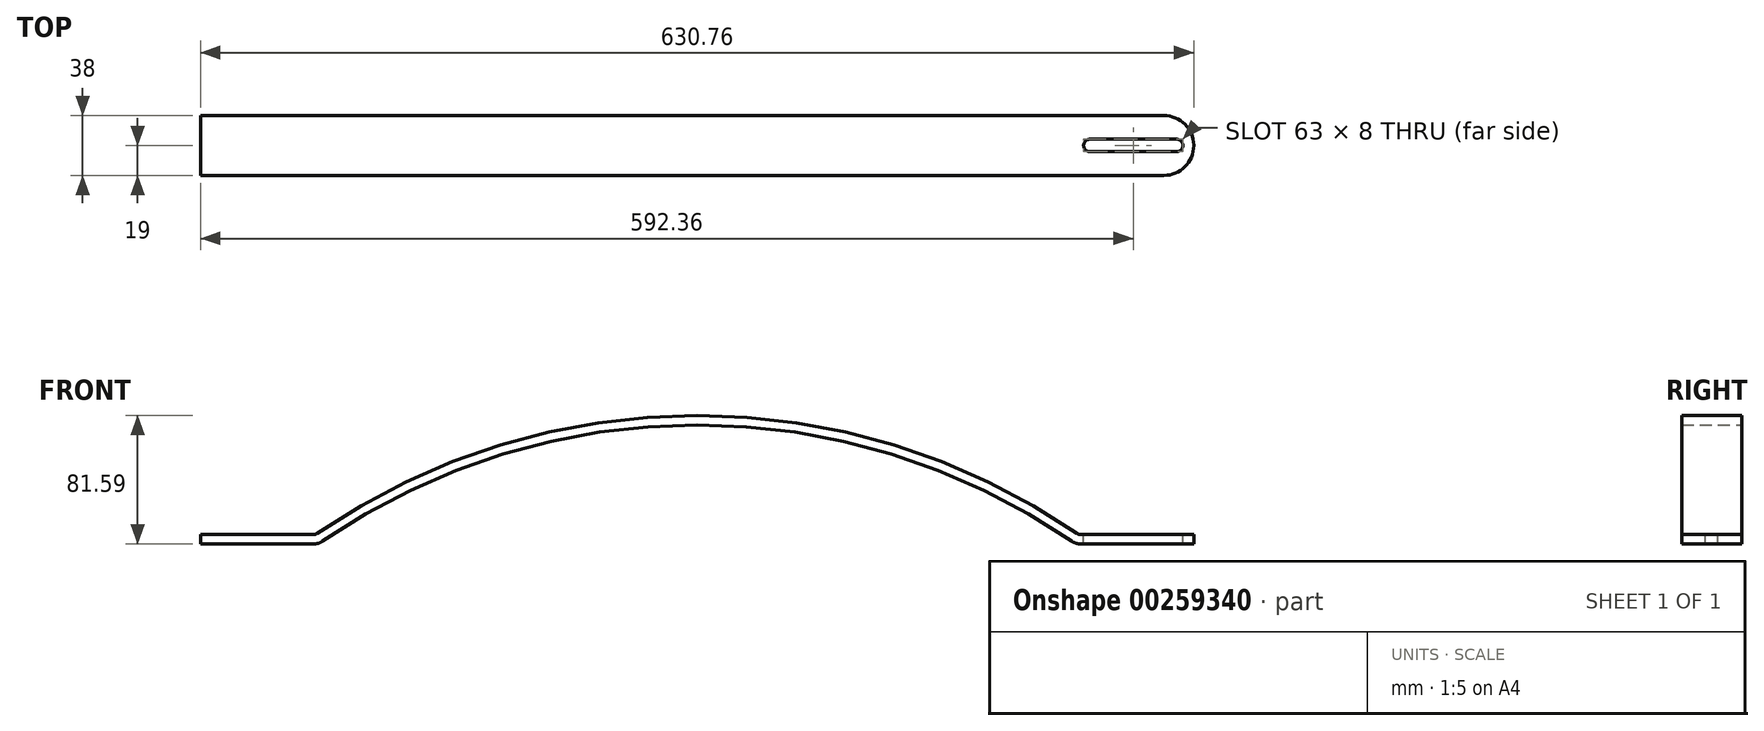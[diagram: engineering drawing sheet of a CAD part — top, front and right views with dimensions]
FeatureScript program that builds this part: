
annotation { "Feature Type Name" : "Feature", "Feature Type Description" : "" }
export const myFeature = defineFeature(function(context is Context, id is Id, definition is map)
    precondition{}
    {
        {
            var Q0;
            Q0=qCreatedBy(makeId("Front.planeOp"),FACE);
            var sketch = newSketch(context, id + "F0", { "sketchPlane" : qUnion([Q0])});
            skLineSegment(sketch, "E0", {"start": v(0, 0) * mm, "end": v(0, -344.41) * mm});
            skArc(sketch, "E1", {"start": v(237.84, 1.76) * mm, "mid": v(0, 75.59) * mm, "end": v(-237.84, 1.76) * mm});
            skLineSegment(sketch, "E2", {"start": v(243.5, 0) * mm, "end": v(315.38, 0) * mm});
            skPoint(sketch, "E3.visualSharp", {"position": v(240.38, 0) * mm});
            skArc(sketch, "E3.filletArc", {"start": v(237.84, 1.76) * mm, "mid": v(240.54, 0.45) * mm, "end": v(243.5, 0) * mm});
            skArc(sketch, "E4.MirrorCS", {"start": v(-237.84, 1.76) * mm, "mid": v(-240.54, 0.45) * mm, "end": v(-243.5, 0) * mm});
            skPoint(sketch, "E5.MirrorP", {"position": v(-240.38, 0) * mm});
            skArc(sketch, "E6.0", {"start": v(241.24, 6.7) * mm, "mid": v(0, 81.59) * mm, "end": v(-241.24, 6.7) * mm});
            skArc(sketch, "E6.1", {"start": v(241.24, 6.7) * mm, "mid": v(242.32, 6.18) * mm, "end": v(243.5, 6) * mm});
            skLineSegment(sketch, "E6.2", {"start": v(243.5, 6) * mm, "end": v(315.38, 6) * mm});
            skLineSegment(sketch, "E7.MirrorCS", {"start": v(-243.5, 0) * mm, "end": v(-315.38, 0) * mm});
            skLineSegment(sketch, "E8.MirrorCS", {"start": v(-243.5, 6) * mm, "end": v(-315.38, 6) * mm});
            skArc(sketch, "E9.MirrorCS", {"start": v(-241.24, 6.7) * mm, "mid": v(-242.32, 6.18) * mm, "end": v(-243.5, 6) * mm});
            skLineSegment(sketch, "E10", {"start": v(315.38, 6) * mm, "end": v(315.38, 0) * mm});
            skLineSegment(sketch, "E11", {"start": v(-315.38, 6) * mm, "end": v(-315.38, 0) * mm});
            skSolve(sketch);
        }
        {
            var Q0;
            Q0=makeQuery(id+"F0.imprint","IMPRINT",FACE,{"disambiguationData":[TD([[makeQuery(id+"F0.imprint","IMPRINT",EDGE,{"derivedFrom":sQuery(id+"F0.wireOp",EDGE,"E1")}),-1.0]])]});
            extrude(context, id + "F1", {"entities" : qUnion([Q0]), "endBound" : BoundingType.SYMMETRIC, "depth" : 38 * mm});
        }
        {
            var Q0;
            Q0=makeQuery(id+"F1.opExtrude","SWEPT_FACE",FACE,{"disambiguationData":[OSD([sQuery(id+"F0.wireOp",EDGE,"E7.MirrorCS")])]});
            var sketch = newSketch(context, id + "F2", { "sketchPlane" : qUnion([Q0])});
            skLineSegment(sketch, "E12", {"start": v(315.2, 0) * mm, "end": v(274.42, 0) * mm, "construction": true});
            skLineSegment(sketch, "E13", {"start": v(296.38, 19) * mm, "end": v(315.38, 19) * mm});
            skLineSegment(sketch, "E14.MirrorCS", {"start": v(296.38, -19) * mm, "end": v(315.64, -19) * mm});
            skLineSegment(sketch, "E15", {"start": v(296.2, 0) * mm, "end": v(296.38, 0) * mm});
            skLineSegment(sketch, "E16", {"start": v(296.38, 0) * mm, "end": v(296.38, 2.11) * mm});
            skArc(sketch, "E17", {"start": v(296.38, -19) * mm, "mid": v(315.38, 0) * mm, "end": v(296.38, 19) * mm});
            skLineSegment(sketch, "E18", {"start": v(296.38, 0) * mm, "end": v(296.38, -20.72) * mm, "construction": true});
            skPoint(sketch, "E19.orphan", {"position": v(296.38, -19) * mm});
            skLineSegment(sketch, "E20", {"start": v(296.38, 0) * mm, "end": v(296.38, 20.15) * mm, "construction": true});
            skLineSegment(sketch, "E21", {"start": v(315.38, 0) * mm, "end": v(315.38, 19) * mm});
            skLineSegment(sketch, "E22.MirrorCS", {"start": v(315.38, 0) * mm, "end": v(315.38, -19) * mm});
            skSolve(sketch);
        }
        {
            var Q0;
            {var subQ0=sQuery(id+"F2.wireOp",EDGE,"E13");var subQ1=sQuery(id+"F2.wireOp",EDGE,"DCdSjiAZ-xsdK-Wht0-eUJy-N4OGyVzoxLP8");var subQ2=makeQuery(id+"F2.imprint","INTERSECT",VERTEX,{"derivedFrom":[subQ1,subQ0]});Q0=makeQuery(id+"F2.imprint","IMPRINT",FACE,{"disambiguationData":[TD([[makeQuery(id+"F2.imprint","IMPRINT",EDGE,{"disambiguationData":[TD([[subQ2,-1.0]])],"derivedFrom":subQ0}),-1.0]])]});}
            var Q1;
            {var subQ0=sQuery(id+"F2.wireOp",EDGE,"E14.MirrorCS");var subQ1=sQuery(id+"F2.wireOp",EDGE,"DCdSjiAZ-xsdK-Wht0-eUJy-N4OGyVzoxLP8");var subQ2=makeQuery(id+"F2.imprint","INTERSECT",VERTEX,{"derivedFrom":[subQ1,subQ0]});Q1=makeQuery(id+"F2.imprint","IMPRINT",FACE,{"disambiguationData":[TD([[makeQuery(id+"F2.imprint","IMPRINT",EDGE,{"disambiguationData":[TD([[subQ2,-1.0]])],"derivedFrom":subQ0}),1.0]])]});}
            extrude(context, id + "F3", {"entities" : qUnion([Q0, Q1]), "operationType" : NewBodyOperationType.REMOVE, "oppositeDirection" : true, "depth" : 25 * mm});
        }
        {
            var Q0;
            Q0=makeQuery(id+"F1.opExtrude","SWEPT_FACE",FACE,{"disambiguationData":[OSD([sQuery(id+"F0.wireOp",EDGE,"E6.2")])]});
            cPlane(context, id + "F4", {"entities" : qUnion([Q0]), "cplaneType" : CPlaneType.OFFSET, "offset" : 0 * mm, "width" : 150 * mm, "height" : 150 * mm});
        }
        {
            var Q0;
            Q0=qCreatedBy(id+"F4.planeOp",FACE);
            var sketch = newSketch(context, id + "F5", { "sketchPlane" : qUnion([Q0])});
            skLineSegment(sketch, "E23", {"start": v(325.27, 0) * mm, "end": v(235.2, 0) * mm, "construction": true});
            skLineSegment(sketch, "E24", {"start": v(249.48, 0) * mm, "end": v(249.48, 4) * mm, "construction": true});
            skLineSegment(sketch, "E25", {"start": v(249.48, 0) * mm, "end": v(304.48, 0) * mm});
            skLineSegment(sketch, "E26", {"start": v(304.48, 0) * mm, "end": v(304.48, 4) * mm, "construction": true});
            skLineSegment(sketch, "E27", {"start": v(304.48, 4) * mm, "end": v(249.48, 4) * mm});
            skLineSegment(sketch, "E28", {"start": v(249.48, 0) * mm, "end": v(249.48, 4) * mm});
            skLineSegment(sketch, "E29.trimOffspring", {"start": v(249.48, 6.72) * mm, "end": v(249.48, 47.13) * mm, "construction": true});
            skLineSegment(sketch, "E30.MirrorCS", {"start": v(304.48, -4) * mm, "end": v(249.48, -4) * mm});
            skLineSegment(sketch, "E31.MirrorCS", {"start": v(304.48, 0) * mm, "end": v(304.48, -4) * mm, "construction": true});
            skLineSegment(sketch, "E32.MirrorCS", {"start": v(249.48, 0) * mm, "end": v(249.48, -4) * mm, "construction": true});
            skArc(sketch, "E33", {"start": v(304.48, 4) * mm, "mid": v(308.48, 0) * mm, "end": v(304.48, -4) * mm});
            skArc(sketch, "E34", {"start": v(249.48, -4) * mm, "mid": v(245.48, 0) * mm, "end": v(249.48, 4) * mm});
            skSolve(sketch);
        }
        {
            var Q0;
            Q0=makeQuery(id+"F5.imprint","IMPRINT",FACE,{"disambiguationData":[TD([[makeQuery(id+"F5.imprint","IMPRINT",EDGE,{"derivedFrom":sQuery(id+"F5.wireOp",EDGE,"E27")}),1.0]])]});
            extrude(context, id + "F6", {"entities" : qUnion([Q0]), "operationType" : NewBodyOperationType.REMOVE, "endBound" : BoundingType.THROUGH_ALL, "oppositeDirection" : true, "depth" : 25 * mm});
        }
    });
